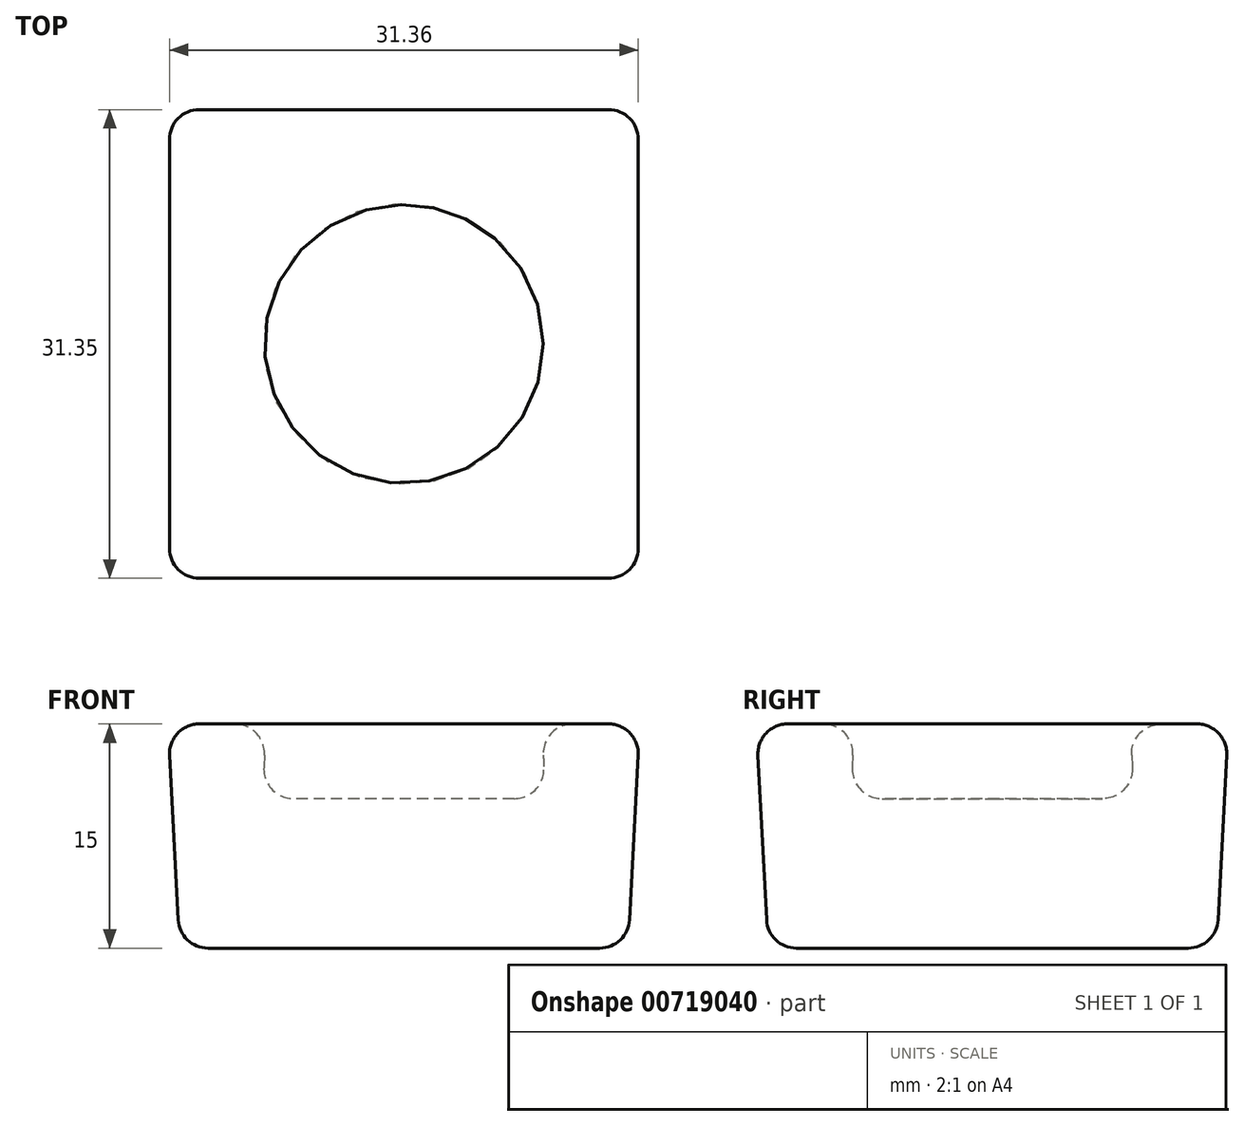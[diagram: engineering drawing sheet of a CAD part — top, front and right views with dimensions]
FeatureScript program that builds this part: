
annotation { "Feature Type Name" : "Feature", "Feature Type Description" : "" }
export const myFeature = defineFeature(function(context is Context, id is Id, definition is map)
    precondition{}
    {
        {
            var Q0;
            Q0=qCreatedBy(makeId("Top.planeOp"),FACE);
            var sketch = newSketch(context, id + "F0", { "sketchPlane" : qUnion([Q0])});
            skLineSegment(sketch, "E0.bottom", {"start": v(-73.32, -40.53) * mm, "end": v(-43.32, -40.53) * mm});
            skLineSegment(sketch, "E0.top", {"start": v(-73.32, -70.53) * mm, "end": v(-43.32, -70.53) * mm});
            skLineSegment(sketch, "E0.left", {"start": v(-73.32, -40.53) * mm, "end": v(-73.32, -70.53) * mm});
            skLineSegment(sketch, "E0.right", {"start": v(-43.32, -40.53) * mm, "end": v(-43.32, -70.53) * mm});
            skCircle(sketch, "E1", {"center": v(-58.32, -55.53) * mm, "radius": 10 * mm});
            skPoint(sketch, "E1.centerSnap0", {"position": v(-73.32, -55.53) * mm});
            skPoint(sketch, "E1.centerSnap1", {"position": v(-58.32, -40.53) * mm});
            skSolve(sketch);
        }
        {
            var Q0;
            Q0 = qSketchRegion(id + "F0", true);
            extrude(context, id + "F1", {"entities" : qUnion([Q0]), "depth" : 15 * mm, "offsetDistance" : 25 * mm, "hasDraft" : true, "draftAngle" : 3 * degree});
        }
        {
            var Q0;
            Q0=makeQuery(id+"F0.imprint","IMPRINT",FACE,{"disambiguationData":[TD([[makeQuery(id+"F0.imprint","IMPRINT",EDGE,{"derivedFrom":sQuery(id+"F0.wireOp",EDGE,"E1")}),1.0]])]});
            extrude(context, id + "F2", {"entities" : qUnion([Q0]), "operationType" : NewBodyOperationType.ADD, "depth" : 10 * mm, "offsetDistance" : 25 * mm});
        }
        {
            var Q0;
            {var subQ0=sQuery(id+"F0.wireOp",EDGE,"E1");Q0=makeQuery(id+"F2.boolean.opBoolean","INTERSECT",EDGE,{"derivedFrom":[makeQuery(id+"F1.opExtrude","SWEPT_FACE",FACE,{"disambiguationData":[OSD([subQ0])]}),makeQuery(id+"F2.opExtrude","CAP_FACE",FACE,{"disambiguationData":[OSD([subQ0])],"isStart":false})]});}
            var Q1;
            Q1=makeQuery(id+"F1.opExtrude","CAP_EDGE",EDGE,{"disambiguationData":[OSD([sQuery(id+"F0.wireOp",EDGE,"E1")])],"isStart":false});
            var Q2;
            Q2=makeQuery(id+"F1.opExtrude","CAP_EDGE",EDGE,{"disambiguationData":[OSD([sQuery(id+"F0.wireOp",EDGE,"E0.right")])],"isStart":false});
            var Q3;
            Q3=makeQuery(id+"F1.opExtrude","CAP_FACE",FACE,{"disambiguationData":[OSD([sQuery(id+"F0.wireOp",EDGE,"E0.bottom"),sQuery(id+"F0.wireOp",EDGE,"E0.top"),sQuery(id+"F0.wireOp",EDGE,"E0.left"),sQuery(id+"F0.wireOp",EDGE,"E0.right"),sQuery(id+"F0.wireOp",EDGE,"E1")])],"isStart":false});
            var Q4;
            {var subQ0=sQuery(id+"F0.wireOp",EDGE,"E1");Q4=makeQuery(id+"F2.boolean.opBoolean","MERGE",FACE,{"derivedFrom":[makeQuery(id+"F1.opExtrude","CAP_FACE",FACE,{"disambiguationData":[OSD([sQuery(id+"F0.wireOp",EDGE,"E0.bottom"),sQuery(id+"F0.wireOp",EDGE,"E0.top"),sQuery(id+"F0.wireOp",EDGE,"E0.left"),sQuery(id+"F0.wireOp",EDGE,"E0.right"),subQ0])],"isStart":true}),makeQuery(id+"F2.opExtrude","CAP_FACE",FACE,{"disambiguationData":[OSD([subQ0])],"isStart":true})]});}
            var Q5;
            Q5=makeQuery(id+"F1.opExtrude","SWEPT_EDGE",EDGE,{"disambiguationData":[OSD([sQuery(id+"F0.wireOp",EDGE,"E0.top"),sQuery(id+"F0.wireOp",EDGE,"E0.right")])]});
            var Q6;
            Q6=makeQuery(id+"F1.opExtrude","SWEPT_FACE",FACE,{"disambiguationData":[OSD([sQuery(id+"F0.wireOp",EDGE,"E0.right")])]});
            var Q7;
            Q7=makeQuery(id+"F1.opExtrude","SWEPT_EDGE",EDGE,{"disambiguationData":[OSD([sQuery(id+"F0.wireOp",EDGE,"E0.top"),sQuery(id+"F0.wireOp",EDGE,"E0.left")])]});
            var Q8;
            Q8=makeQuery(id+"F1.opExtrude","SWEPT_EDGE",EDGE,{"disambiguationData":[OSD([sQuery(id+"F0.wireOp",EDGE,"E0.bottom"),sQuery(id+"F0.wireOp",EDGE,"E0.left")])]});
            fillet(context, id + "F3", {"entities" : qUnion([Q0, Q1, Q2, Q3, Q4, Q5, Q6, Q7, Q8]), "radius" : 2 * mm, "tangentPropagation" : true, "allowEdgeOverflow" : false});
        }
    });
